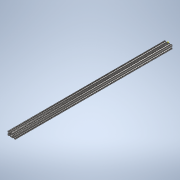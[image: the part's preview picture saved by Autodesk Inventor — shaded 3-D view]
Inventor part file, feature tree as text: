
AUTODESK INVENTOR PART (.ipt)
format: ipt  version: 2020 (Build 240168000, 168)  size: 349,184 bytes
history: native  units: in
note: dims shown in document units (in); Inventor stores cm internally (conversion verified against a paired STEP export)
features: sketch x2, extrude x1
ambient origin geometry x8: Origin, YZ Plane, XZ Plane, XY Plane, X Axis, Y Axis, Z Axis, Center Point
bodies: Solid1 (feature_tree)
feature tree (3):
  extrude  "Extrusion1"  [1 undecoded]
  sketch  "Sketch2"
  sketch  "Sketch1"  dims[d0=40.0in d1=0.0in]
note: 1 required parameter value undecoded (feature->parameter linkage not recoverable at this tier; creation-order binding heuristic only, values carry confidence <= 0.55)
